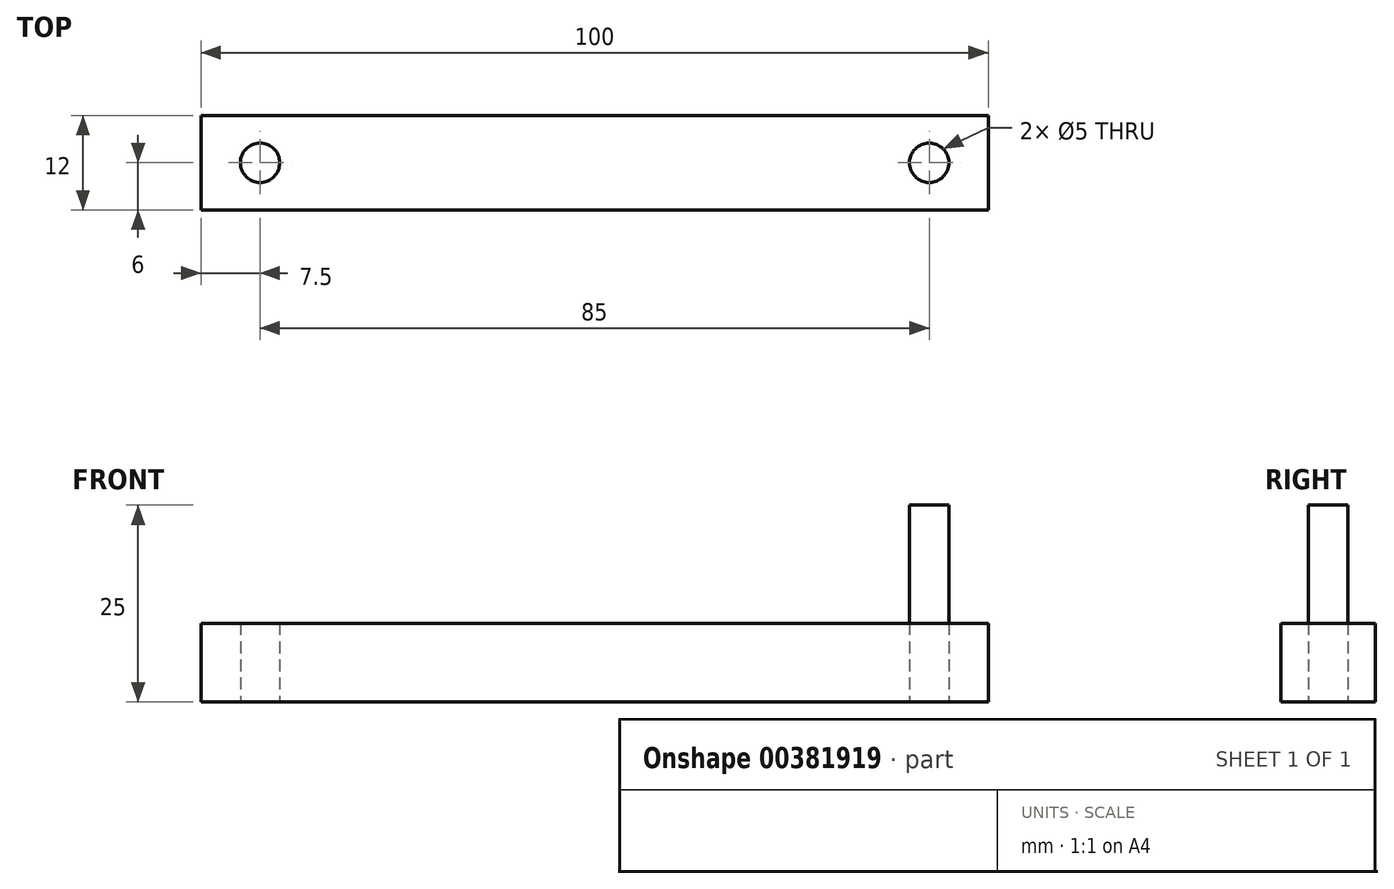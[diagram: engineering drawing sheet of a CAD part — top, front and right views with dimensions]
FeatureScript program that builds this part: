
annotation { "Feature Type Name" : "Feature", "Feature Type Description" : "" }
export const myFeature = defineFeature(function(context is Context, id is Id, definition is map)
    precondition{}
    {
        {
            var Q0;
            Q0=qCreatedBy(makeId("Top.planeOp"),FACE);
            var sketch = newSketch(context, id + "F0", { "sketchPlane" : qUnion([Q0])});
            skLineSegment(sketch, "E0.bottom", {"start": v(0, 0) * mm, "end": v(160, 0) * mm, "construction": true});
            skLineSegment(sketch, "E0.top", {"start": v(0, 80) * mm, "end": v(160, 80) * mm, "construction": true});
            skLineSegment(sketch, "E0.left", {"start": v(0, 0) * mm, "end": v(0, 80) * mm, "construction": true});
            skLineSegment(sketch, "E0.right", {"start": v(160, 0) * mm, "end": v(160, 80) * mm, "construction": true});
            skArc(sketch, "E1", {"start": v(15, 20) * mm, "mid": v(10, 15) * mm, "end": v(15, 10) * mm, "construction": true});
            skLineSegment(sketch, "E2", {"start": v(0, 15) * mm, "end": v(160, 15) * mm, "construction": true});
            skArc(sketch, "E3", {"start": v(145, 10) * mm, "mid": v(150, 15) * mm, "end": v(145, 20) * mm, "construction": true});
            skLineSegment(sketch, "E4", {"start": v(15, 20) * mm, "end": v(145, 20) * mm, "construction": true});
            skLineSegment(sketch, "E5", {"start": v(145, 10) * mm, "end": v(15, 10) * mm, "construction": true});
            skCircle(sketch, "E6", {"center": v(130, 50) * mm, "radius": 4 * mm});
            skCircle(sketch, "E7", {"center": v(130, 50) * mm, "radius": 17.5 * mm});
            skArc(sketch, "E8", {"start": v(20, 55) * mm, "mid": v(15, 50) * mm, "end": v(20, 45) * mm, "construction": true});
            skArc(sketch, "E9", {"start": v(46, 45) * mm, "mid": v(51, 50) * mm, "end": v(46, 55) * mm, "construction": true});
            skLineSegment(sketch, "E10", {"start": v(20, 50) * mm, "end": v(46, 50) * mm, "construction": true});
            skLineSegment(sketch, "E11", {"start": v(20, 55) * mm, "end": v(46, 55) * mm, "construction": true});
            skLineSegment(sketch, "E12", {"start": v(20, 45) * mm, "end": v(46, 45) * mm, "construction": true});
            skLineSegment(sketch, "E13.bottom", {"start": v(0, 0) * mm, "end": v(30, 0) * mm});
            skLineSegment(sketch, "E13.top", {"start": v(0, 32.5) * mm, "end": v(30, 32.5) * mm});
            skLineSegment(sketch, "E13.left", {"start": v(0, 0) * mm, "end": v(0, 32.5) * mm});
            skLineSegment(sketch, "E13.right", {"start": v(30, 0) * mm, "end": v(30, 32.5) * mm});
            skCircle(sketch, "E14", {"center": v(15, 15) * mm, "radius": 5 * mm});
            skLineSegment(sketch, "E15", {"start": v(30, 32.5) * mm, "end": v(160, 32.5) * mm});
            skLineSegment(sketch, "E16", {"start": v(160, 32.5) * mm, "end": v(160, 22.5) * mm});
            skLineSegment(sketch, "E17", {"start": v(160, 22.5) * mm, "end": v(30, 22.5) * mm});
            skCircle(sketch, "E18", {"center": v(143, 50) * mm, "radius": 2.5 * mm});
            skLineSegment(sketch, "E19.bottom", {"start": v(73.5, 62.5) * mm, "end": v(18.5, 62.5) * mm});
            skLineSegment(sketch, "E19.top", {"start": v(73.5, 37.5) * mm, "end": v(18.5, 37.5) * mm});
            skLineSegment(sketch, "E19.left", {"start": v(73.5, 62.5) * mm, "end": v(73.5, 37.5) * mm});
            skLineSegment(sketch, "E19.right", {"start": v(18.5, 62.5) * mm, "end": v(18.5, 37.5) * mm});
            skCircle(sketch, "E20", {"center": v(58, 50) * mm, "radius": 2.5 * mm});
            skCircle(sketch, "E21", {"center": v(46, 50) * mm, "radius": 5 * mm});
            skLineSegment(sketch, "E22.bottom", {"start": v(50.5, 44) * mm, "end": v(150.5, 44) * mm});
            skLineSegment(sketch, "E22.top", {"start": v(50.5, 56) * mm, "end": v(150.5, 56) * mm});
            skLineSegment(sketch, "E22.left", {"start": v(50.5, 44) * mm, "end": v(50.5, 56) * mm});
            skLineSegment(sketch, "E22.right", {"start": v(150.5, 44) * mm, "end": v(150.5, 56) * mm});
            skPoint(sketch, "E22.middle", {"position": v(100.5, 50) * mm});
            skSolve(sketch);
        }
        {
            var Q0;
            Q0=makeQuery(id+"F0.imprint","IMPRINT",FACE,{"disambiguationData":[TD([[makeQuery(id+"F0.imprint","IMPRINT",EDGE,{"derivedFrom":sQuery(id+"F0.wireOp",EDGE,"E20")}),-1.0]])]});
            var Q1;
            {var subQ0=sQuery(id+"F0.wireOp",EDGE,"E22.top");var subQ1=sQuery(id+"F0.wireOp",EDGE,"E7");var subQ2=makeQuery(id+"F0.imprint","INTERSECT",VERTEX,{"disambiguationData":[OD(0.0)],"derivedFrom":[subQ1,subQ0]});Q1=makeQuery(id+"F0.imprint","IMPRINT",FACE,{"disambiguationData":[TD([[makeQuery(id+"F0.imprint","IMPRINT",EDGE,{"disambiguationData":[TD([[subQ2,-1.0]])],"derivedFrom":subQ1}),-1.0]])]});}
            var Q2;
            Q2=makeQuery(id+"F0.imprint","IMPRINT",FACE,{"disambiguationData":[TD([[makeQuery(id+"F0.imprint","IMPRINT",EDGE,{"derivedFrom":sQuery(id+"F0.wireOp",EDGE,"E6")}),-1.0]])]});
            var Q3;
            {var subQ5=sQuery(id+"F0.wireOp",EDGE,"E22.right");Q3=makeQuery(id+"F0.imprint","IMPRINT",FACE,{"disambiguationData":[TD([[makeQuery(id+"F0.imprint","IMPRINT",EDGE,{"derivedFrom":subQ5}),1.0]])]});}
            var Q4;
            Q4=makeQuery(id+"F0.imprint","IMPRINT",FACE,{"disambiguationData":[TD([[makeQuery(id+"F0.imprint","IMPRINT",EDGE,{"derivedFrom":sQuery(id+"F0.wireOp",EDGE,"E6")}),1.0]])]});
            var Q5;
            {var subQ0=sQuery(id+"F0.wireOp",EDGE,"E22.left");var subQ1=sQuery(id+"F0.wireOp",EDGE,"E21");var subQ2=makeQuery(id+"F0.imprint","INTERSECT",VERTEX,{"disambiguationData":[OD(0.0)],"derivedFrom":[subQ1,subQ0]});Q5=makeQuery(id+"F0.imprint","IMPRINT",FACE,{"disambiguationData":[TD([[makeQuery(id+"F0.imprint","IMPRINT",EDGE,{"disambiguationData":[TD([[subQ2,-1.0]])],"derivedFrom":subQ1}),1.0]])]});}
            extrude(context, id + "F1", {"entities" : qUnion([Q0, Q1, Q2, Q3, Q4, Q5]), "depth" : (10) * mm});
        }
        {
            var Q0;
            Q0=makeQuery(id+"F0.imprint","IMPRINT",FACE,{"disambiguationData":[TD([[makeQuery(id+"F0.imprint","IMPRINT",EDGE,{"derivedFrom":sQuery(id+"F0.wireOp",EDGE,"E18")}),1.0]])]});
            extrude(context, id + "F2", {"entities" : qUnion([Q0]), "depth" : 25 * mm});
        }
    });
